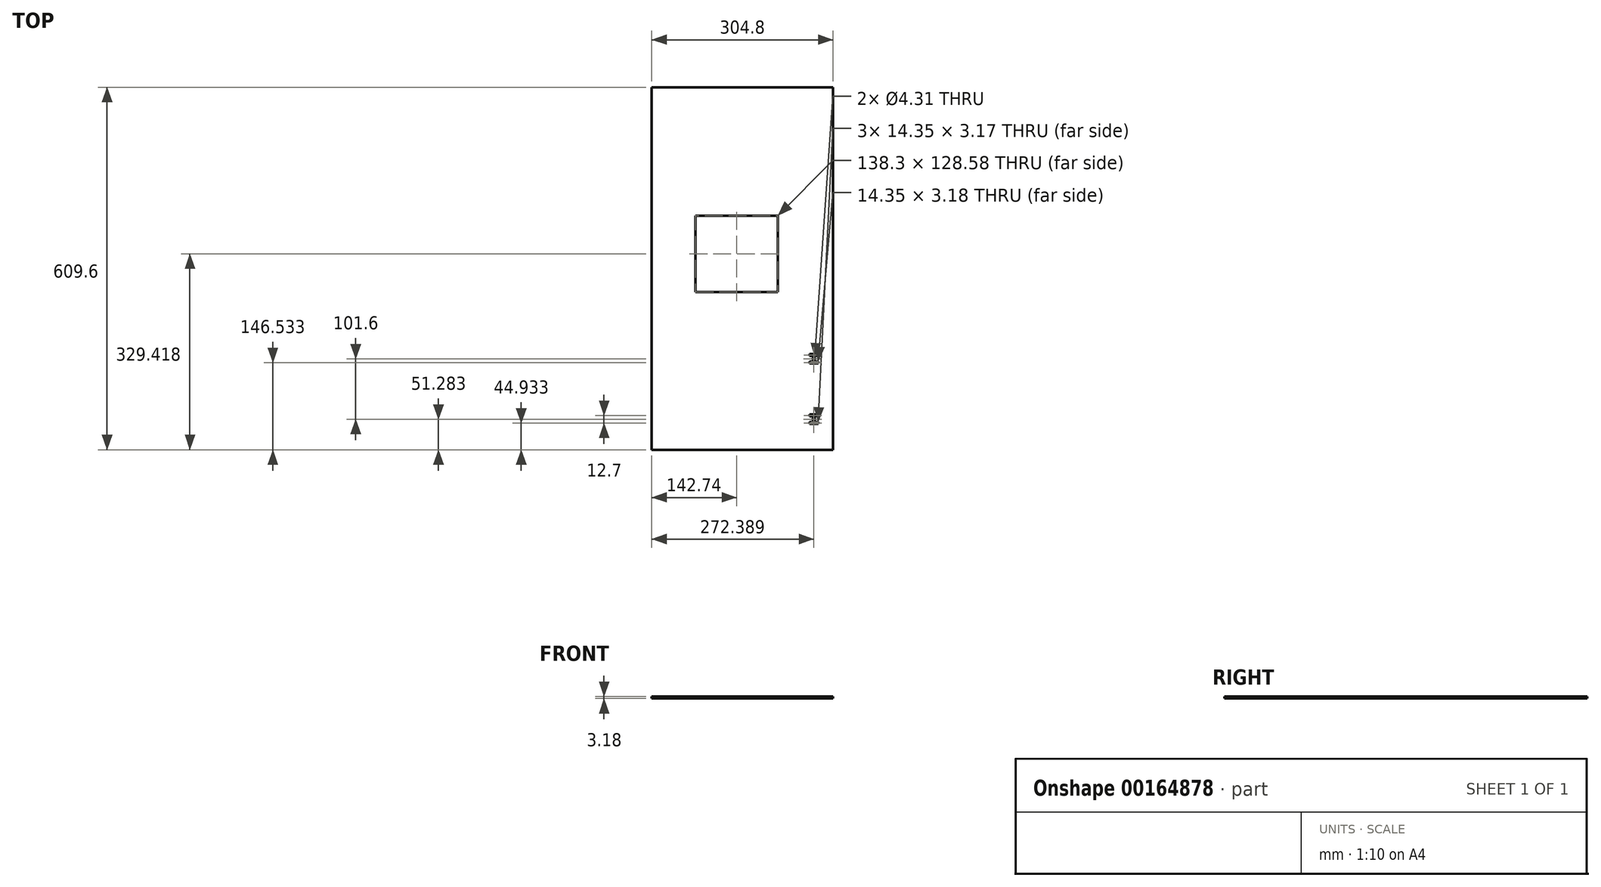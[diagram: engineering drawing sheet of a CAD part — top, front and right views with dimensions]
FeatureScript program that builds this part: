
annotation { "Feature Type Name" : "Feature", "Feature Type Description" : "" }
export const myFeature = defineFeature(function(context is Context, id is Id, definition is map)
    precondition{}
    {
        {
            var Q0;
            Q0=qCreatedBy(makeId("Top.planeOp"),FACE);
            var sketch = newSketch(context, id + "F0", { "sketchPlane" : qUnion([Q0])});
            skLineSegment(sketch, "E0.bottom", {"start": v(0, 0) * mm, "end": v(304.8, 0) * mm});
            skLineSegment(sketch, "E0.top", {"start": v(0, 609.6) * mm, "end": v(304.8, 609.6) * mm});
            skLineSegment(sketch, "E0.left", {"start": v(0, 0) * mm, "end": v(0, 609.6) * mm});
            skLineSegment(sketch, "E1.bottom", {"start": v(279.56, 160.82) * mm, "end": v(265.21, 160.82) * mm});
            skLineSegment(sketch, "E1.top", {"start": v(279.56, 157.65) * mm, "end": v(265.21, 157.65) * mm});
            skLineSegment(sketch, "E1.left", {"start": v(279.56, 160.82) * mm, "end": v(279.56, 157.65) * mm});
            skLineSegment(sketch, "E1.right", {"start": v(265.21, 160.82) * mm, "end": v(265.21, 157.65) * mm});
            skLineSegment(sketch, "E2.bottom", {"start": v(279.56, 148.12) * mm, "end": v(265.21, 148.12) * mm});
            skLineSegment(sketch, "E2.top", {"start": v(279.56, 144.95) * mm, "end": v(265.21, 144.95) * mm});
            skLineSegment(sketch, "E2.left", {"start": v(279.56, 148.12) * mm, "end": v(279.56, 144.95) * mm});
            skLineSegment(sketch, "E2.right", {"start": v(265.21, 148.12) * mm, "end": v(265.21, 144.95) * mm});
            skLineSegment(sketch, "E3.bottom", {"start": v(279.56, 59.22) * mm, "end": v(265.21, 59.22) * mm});
            skLineSegment(sketch, "E3.top", {"start": v(279.56, 56.05) * mm, "end": v(265.21, 56.05) * mm});
            skLineSegment(sketch, "E3.left", {"start": v(279.56, 59.22) * mm, "end": v(279.56, 56.05) * mm});
            skLineSegment(sketch, "E3.right", {"start": v(265.21, 59.22) * mm, "end": v(265.21, 56.05) * mm});
            skLineSegment(sketch, "E4.bottom", {"start": v(279.56, 46.52) * mm, "end": v(265.21, 46.52) * mm});
            skLineSegment(sketch, "E4.top", {"start": v(279.56, 43.35) * mm, "end": v(265.21, 43.35) * mm});
            skLineSegment(sketch, "E4.left", {"start": v(279.56, 46.52) * mm, "end": v(279.56, 43.35) * mm});
            skLineSegment(sketch, "E4.right", {"start": v(265.21, 46.52) * mm, "end": v(265.21, 43.35) * mm});
            skLineSegment(sketch, "E5", {"start": v(272.39, 157.65) * mm, "end": v(272.39, 148.12) * mm, "construction": true});
            skLineSegment(sketch, "E6", {"start": v(272.39, 144.95) * mm, "end": v(272.39, 59.22) * mm, "construction": true});
            skLineSegment(sketch, "E7", {"start": v(272.39, 56.05) * mm, "end": v(272.39, 46.52) * mm, "construction": true});
            skCircle(sketch, "E8", {"center": v(272.39, 152.88) * mm, "radius": 2.15 * mm});
            skCircle(sketch, "E9", {"center": v(272.39, 51.28) * mm, "radius": 2.15 * mm});
            skLineSegment(sketch, "E10", {"start": v(272.39, 102.08) * mm, "end": v(304.8, 102.08) * mm, "construction": true});
            skLineSegment(sketch, "E11", {"start": v(304.8, 0) * mm, "end": v(304.8, 609.6) * mm});
            skLineSegment(sketch, "E12.bottom", {"start": v(73.6, 393.7) * mm, "end": v(211.89, 393.7) * mm});
            skLineSegment(sketch, "E12.top", {"start": v(73.6, 265.13) * mm, "end": v(211.89, 265.13) * mm});
            skLineSegment(sketch, "E12.left", {"start": v(73.6, 393.7) * mm, "end": v(73.6, 265.13) * mm});
            skLineSegment(sketch, "E12.right", {"start": v(211.89, 393.7) * mm, "end": v(211.89, 265.13) * mm});
            skSolve(sketch);
        }
        {
            var Q0;
            Q0=qSketchRegion(id+"F0",true);
            extrude(context, id + "F1", {"entities" : qUnion([Q0]), "depth" : 3.17 * mm});
        }
    });
